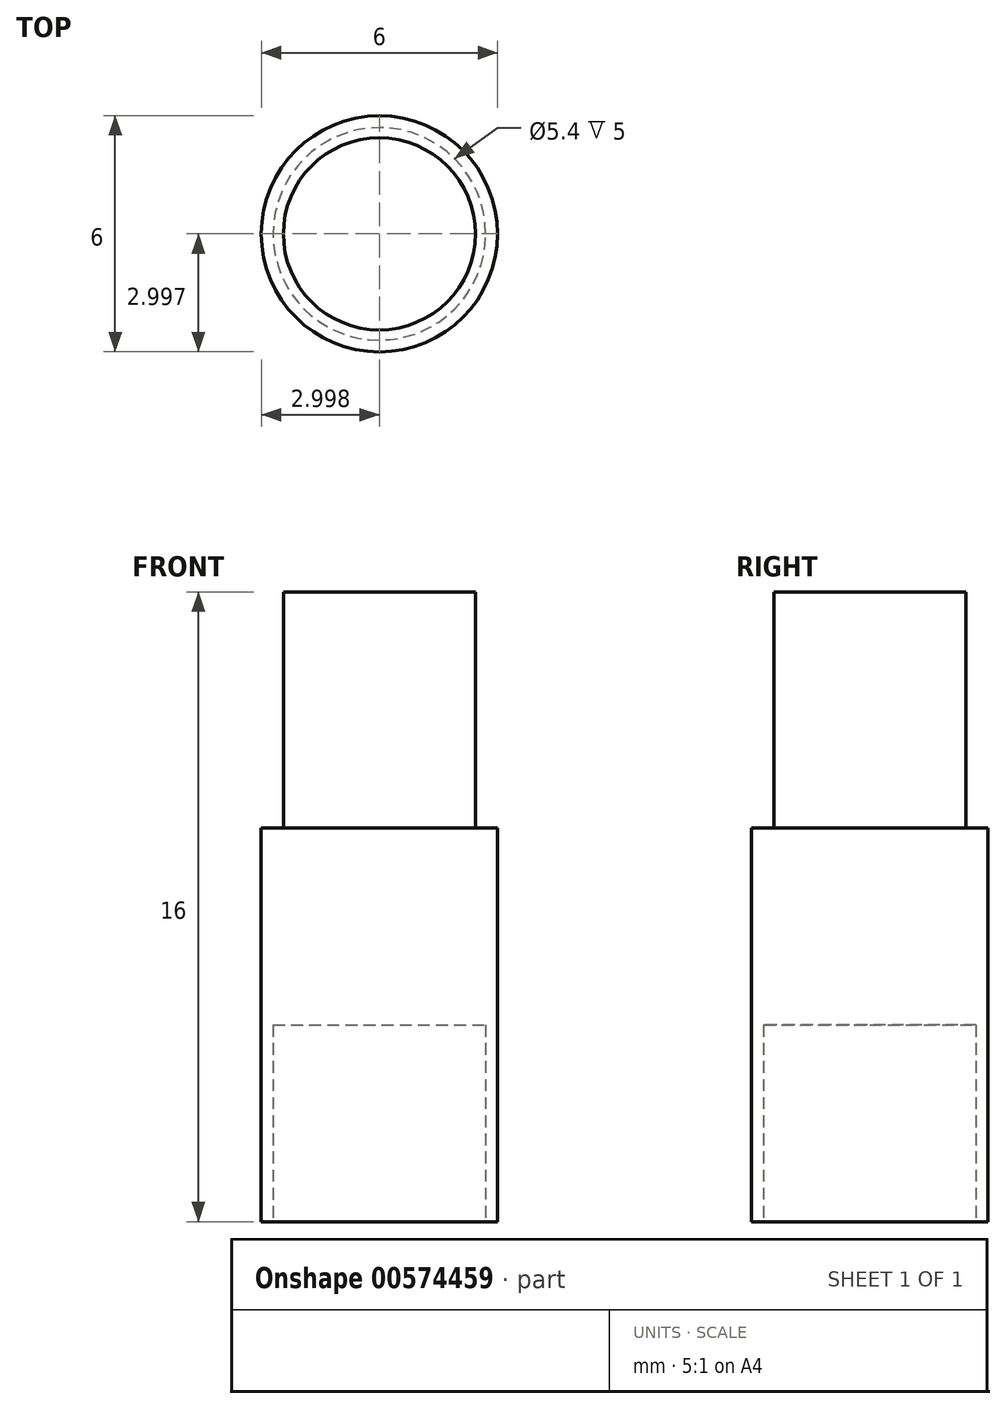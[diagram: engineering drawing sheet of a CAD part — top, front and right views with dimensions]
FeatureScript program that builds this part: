
annotation { "Feature Type Name" : "Feature", "Feature Type Description" : "" }
export const myFeature = defineFeature(function(context is Context, id is Id, definition is map)
    precondition{}
    {
        {
            var Q0;
            Q0=qCreatedBy(makeId("Top.planeOp"),FACE);
            var sketch = newSketch(context, id + "F0", { "sketchPlane" : qUnion([Q0])});
            skCircle(sketch, "E0", {"center": v(-39.5, 19.49) * mm, "radius": 3 * mm});
            skSolve(sketch);
        }
        {
            var Q0;
            Q0=qSketchRegion(id+"F0",true);
            extrude(context, id + "F1", {"entities" : qUnion([Q0]), "depth" : 10 * mm, "offsetDistance" : 25 * mm});
        }
        {
            var Q0;
            Q0=makeQuery(id+"F1.opExtrude","CAP_FACE",FACE,{"disambiguationData":[OSD([sQuery(id+"F0.wireOp",EDGE,"E0")])],"isStart":false});
            var sketch = newSketch(context, id + "F2", { "sketchPlane" : qUnion([Q0])});
            skCircle(sketch, "E1", {"center": v(-39.5, 19.49) * mm, "radius": 2.44 * mm});
            skSolve(sketch);
        }
        {
            var Q0;
            Q0=makeQuery(id+"F2.imprint","IMPRINT",FACE,{"disambiguationData":[TD([[makeQuery(id+"F2.imprint","IMPRINT",EDGE,{"derivedFrom":sQuery(id+"F2.wireOp",EDGE,"E1")}),1.0]])]});
            extrude(context, id + "F3", {"entities" : qUnion([Q0]), "operationType" : NewBodyOperationType.ADD, "depth" : 6 * mm, "offsetDistance" : 25 * mm});
        }
        {
            var Q0;
            Q0=makeQuery(id+"F1.opExtrude","CAP_FACE",FACE,{"disambiguationData":[OSD([sQuery(id+"F0.wireOp",EDGE,"E0")])],"isStart":true});
            var sketch = newSketch(context, id + "F4", { "sketchPlane" : qUnion([Q0])});
            skCircle(sketch, "E2", {"center": v(-39.5, -19.49) * mm, "radius": 2.7 * mm});
            skSolve(sketch);
        }
        {
            var Q0;
            Q0 = qSketchRegion(id + "F4", true);
            extrude(context, id + "F5", {"entities" : qUnion([Q0]), "operationType" : NewBodyOperationType.REMOVE, "oppositeDirection" : true, "depth" : 5 * mm, "offsetDistance" : 25 * mm});
        }
    });
